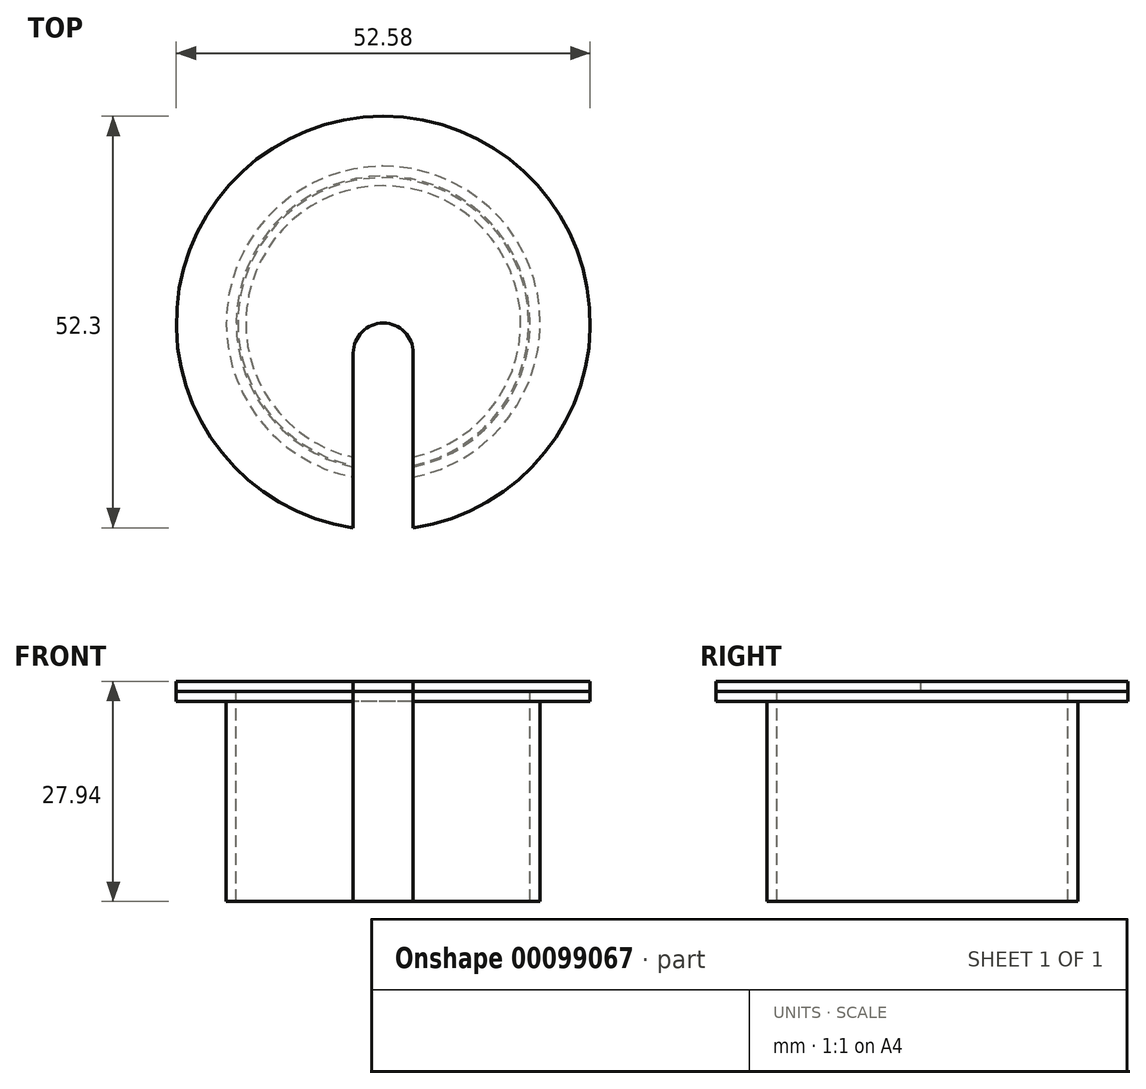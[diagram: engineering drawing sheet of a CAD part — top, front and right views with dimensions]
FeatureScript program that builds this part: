
annotation { "Feature Type Name" : "Feature", "Feature Type Description" : "" }
export const myFeature = defineFeature(function(context is Context, id is Id, definition is map)
    precondition{}
    {
        {
            var Q0;
            Q0=qCreatedBy(makeId("Top.planeOp"),FACE);
            var sketch = newSketch(context, id + "F0", { "sketchPlane" : qUnion([Q0])});
            skCircle(sketch, "E0", {"center": v(0, 0) * mm, "radius": 19.94 * mm});
            skCircle(sketch, "E1.0", {"center": v(0, 0) * mm, "radius": 18.67 * mm});
            skCircle(sketch, "E2.0", {"center": v(0, 0) * mm, "radius": 26.29 * mm});
            skSolve(sketch);
        }
        {
            var Q0;
            Q0=makeQuery(id+"F0.imprint","IMPRINT",FACE,{"disambiguationData":[TD([[makeQuery(id+"F0.imprint","IMPRINT",EDGE,{"derivedFrom":sQuery(id+"F0.wireOp",EDGE,"E0")}),1.0]])]});
            extrude(context, id + "F1", {"entities" : qUnion([Q0]), "oppositeDirection" : true, "depth" : 25.4 * mm});
        }
        {
            var Q0;
            Q0=makeQuery(id+"F0.imprint","IMPRINT",FACE,{"disambiguationData":[TD([[makeQuery(id+"F0.imprint","IMPRINT",EDGE,{"derivedFrom":sQuery(id+"F0.wireOp",EDGE,"E0")}),1.0]])]});
            var Q1;
            Q1=makeQuery(id+"F0.imprint","IMPRINT",FACE,{"disambiguationData":[TD([[makeQuery(id+"F0.imprint","IMPRINT",EDGE,{"derivedFrom":sQuery(id+"F0.wireOp",EDGE,"E0")}),-1.0]])]});
            extrude(context, id + "F2", {"entities" : qUnion([Q0, Q1]), "operationType" : NewBodyOperationType.ADD, "depth" : 1.27 * mm});
        }
        {
            var Q0;
            Q0=makeQuery(id+"F2.opExtrude","CAP_FACE",FACE,{"disambiguationData":[OSD([sQuery(id+"F0.wireOp",EDGE,"E1.0"),sQuery(id+"F0.wireOp",EDGE,"E2.0")])],"isStart":false});
            var sketch = newSketch(context, id + "F3", { "sketchPlane" : qUnion([Q0])});
            skCircle(sketch, "E3", {"center": v(0, 0) * mm, "radius": 26.29 * mm});
            skSolve(sketch);
        }
        {
            var Q0;
            Q0 = qSketchRegion(id + "F3", true);
            extrude(context, id + "F4", {"entities" : qUnion([Q0]), "depth" : 1.27 * mm});
        }
        {
            var Q0;
            Q0=makeQuery(id+"F4.opExtrude","CAP_FACE",FACE,{"disambiguationData":[OSD([sQuery(id+"F3.wireOp",EDGE,"E3")])],"isStart":true});
            var sketch = newSketch(context, id + "F5", { "sketchPlane" : qUnion([Q0])});
            skCircle(sketch, "E4", {"center": v(0, 0) * mm, "radius": 18.47 * mm});
            skCircle(sketch, "E5.0", {"center": v(0, 0) * mm, "radius": 17.45 * mm});
            skSolve(sketch);
        }
        {
            var Q0;
            Q0=makeQuery(id+"F5.imprint","IMPRINT",FACE,{"disambiguationData":[TD([[makeQuery(id+"F5.imprint","IMPRINT",EDGE,{"derivedFrom":sQuery(id+"F5.wireOp",EDGE,"E4")}),1.0]])]});
            extrude(context, id + "F6", {"entities" : qUnion([Q0]), "operationType" : NewBodyOperationType.ADD, "depth" : 1 / 101.6 * mm});
        }
        {
            var Q0;
            Q0=makeQuery(id+"F4.opExtrude","CAP_FACE",FACE,{"disambiguationData":[OSD([sQuery(id+"F3.wireOp",EDGE,"E3")])],"isStart":false});
            var sketch = newSketch(context, id + "F7", { "sketchPlane" : qUnion([Q0])});
            skArc(sketch, "E6", {"start": v(3.81, -3.8) * mm, "mid": v(0, 0) * mm, "end": v(-3.81, -3.81) * mm});
            skLineSegment(sketch, "E7", {"start": v(-3.81, -3.81) * mm, "end": v(-3.8, -26.01) * mm});
            skLineSegment(sketch, "E8", {"start": v(3.81, -3.8) * mm, "end": v(3.81, -26.01) * mm});
            skSolve(sketch);
        }
        {
            var Q0;
            Q0=makeQuery(id+"F7.imprint","IMPRINT",FACE,{"disambiguationData":[TD([[makeQuery(id+"F7.imprint","IMPRINT",EDGE,{"derivedFrom":sQuery(id+"F7.wireOp",EDGE,"E6")}),1.0]])]});
            extrude(context, id + "F8", {"entities" : qUnion([Q0]), "operationType" : NewBodyOperationType.REMOVE, "endBound" : BoundingType.THROUGH_ALL, "oppositeDirection" : true, "depth" : 25.4 * mm});
        }
    });
